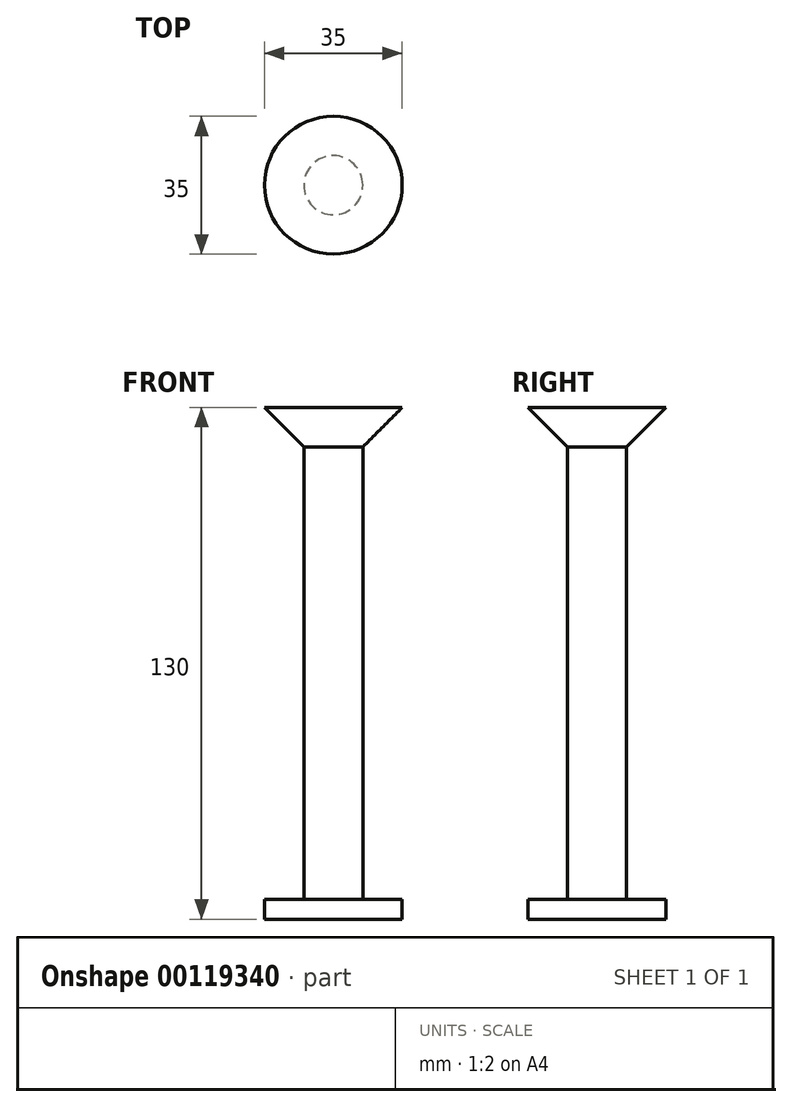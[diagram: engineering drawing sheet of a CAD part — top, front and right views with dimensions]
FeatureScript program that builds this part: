
annotation { "Feature Type Name" : "Feature", "Feature Type Description" : "" }
export const myFeature = defineFeature(function(context is Context, id is Id, definition is map)
    precondition{}
    {
        {
            var Q0;
            Q0=qCreatedBy(makeId("Front.planeOp"),FACE);
            var sketch = newSketch(context, id + "F0", { "sketchPlane" : qUnion([Q0])});
            skLineSegment(sketch, "E0.bottom", {"start": v(-7.5, 60) * mm, "end": v(7.5, 60) * mm});
            skLineSegment(sketch, "E0.top", {"start": v(-7.5, -60) * mm, "end": v(7.5, -60) * mm});
            skLineSegment(sketch, "E0.left", {"start": v(-7.5, 60) * mm, "end": v(-7.5, -60) * mm});
            skLineSegment(sketch, "E0.right", {"start": v(7.5, 60) * mm, "end": v(7.5, -60) * mm});
            skPoint(sketch, "E0.middle", {"position": v(0, 0) * mm});
            skLineSegment(sketch, "E1.bottom", {"start": v(-17.5, 60) * mm, "end": v(17.5, 60) * mm});
            skLineSegment(sketch, "E1.top", {"start": v(-17.5, 65) * mm, "end": v(17.5, 65) * mm});
            skLineSegment(sketch, "E1.left", {"start": v(-17.5, 60) * mm, "end": v(-17.5, 65) * mm});
            skLineSegment(sketch, "E1.right", {"start": v(17.5, 60) * mm, "end": v(17.5, 65) * mm});
            skLineSegment(sketch, "E2", {"start": v(-46.13, 0) * mm, "end": v(50.78, 0) * mm, "construction": true});
            skLineSegment(sketch, "E3.MirrorCS", {"start": v(-17.5, -65) * mm, "end": v(17.5, -65) * mm});
            skLineSegment(sketch, "E4.MirrorCS", {"start": v(-17.5, -60) * mm, "end": v(17.5, -60) * mm});
            skLineSegment(sketch, "E5.MirrorCS", {"start": v(-17.5, -60) * mm, "end": v(-17.5, -65) * mm});
            skLineSegment(sketch, "E6.MirrorCS", {"start": v(17.5, -60) * mm, "end": v(17.5, -65) * mm});
            skLineSegment(sketch, "E7", {"start": v(0, 65) * mm, "end": v(0, -65) * mm});
            skSolve(sketch);
        }
        {
            var Q0;
            {var subQ0=sQuery(id+"F0.wireOp",EDGE,"E1.right");Q0=makeQuery(id+"F0.imprint","IMPRINT",FACE,{"disambiguationData":[TD([[makeQuery(id+"F0.imprint","IMPRINT",EDGE,{"derivedFrom":subQ0}),1.0]])]});}
            var Q1;
            Q1=sQuery(id+"F0.wireOp",EDGE,"E7");
            revolve(context, id + "F1", {"entities" : qUnion([Q0]), "axis" : qUnion([Q1]), "revolveType" : RevolveType.FULL});
        }
        {
            var Q0;
            {var subQ0=sQuery(id+"F0.wireOp",EDGE,"E0.right");Q0=makeQuery(id+"F0.imprint","IMPRINT",FACE,{"disambiguationData":[TD([[makeQuery(id+"F0.imprint","IMPRINT",EDGE,{"derivedFrom":subQ0}),-1.0]])]});}
            var Q1;
            Q1=sQuery(id+"F0.wireOp",EDGE,"E7");
            revolve(context, id + "F2", {"operationType" : NewBodyOperationType.ADD, "entities" : qUnion([Q0]), "axis" : qUnion([Q1]), "revolveType" : RevolveType.FULL});
        }
        {
            var Q0;
            {var subQ0=sQuery(id+"F0.wireOp",EDGE,"E6.MirrorCS");Q0=makeQuery(id+"F0.imprint","IMPRINT",FACE,{"disambiguationData":[TD([[makeQuery(id+"F0.imprint","IMPRINT",EDGE,{"derivedFrom":subQ0}),-1.0]])]});}
            var Q1;
            Q1=sQuery(id+"F0.wireOp",EDGE,"E7");
            revolve(context, id + "F3", {"operationType" : NewBodyOperationType.ADD, "entities" : qUnion([Q0]), "axis" : qUnion([Q1]), "revolveType" : RevolveType.FULL});
        }
        {
            var Q0;
            Q0=makeQuery(id+"F1.opRevolve","SWEPT_FACE",FACE,{"disambiguationData":[OSD([sQuery(id+"F0.wireOp",EDGE,"E1.bottom")])]});
            chamfer(context, id + "F4", {"entities" : qUnion([Q0]), "width" : 5 * mm, "tangentPropagation" : true});
        }
    });
